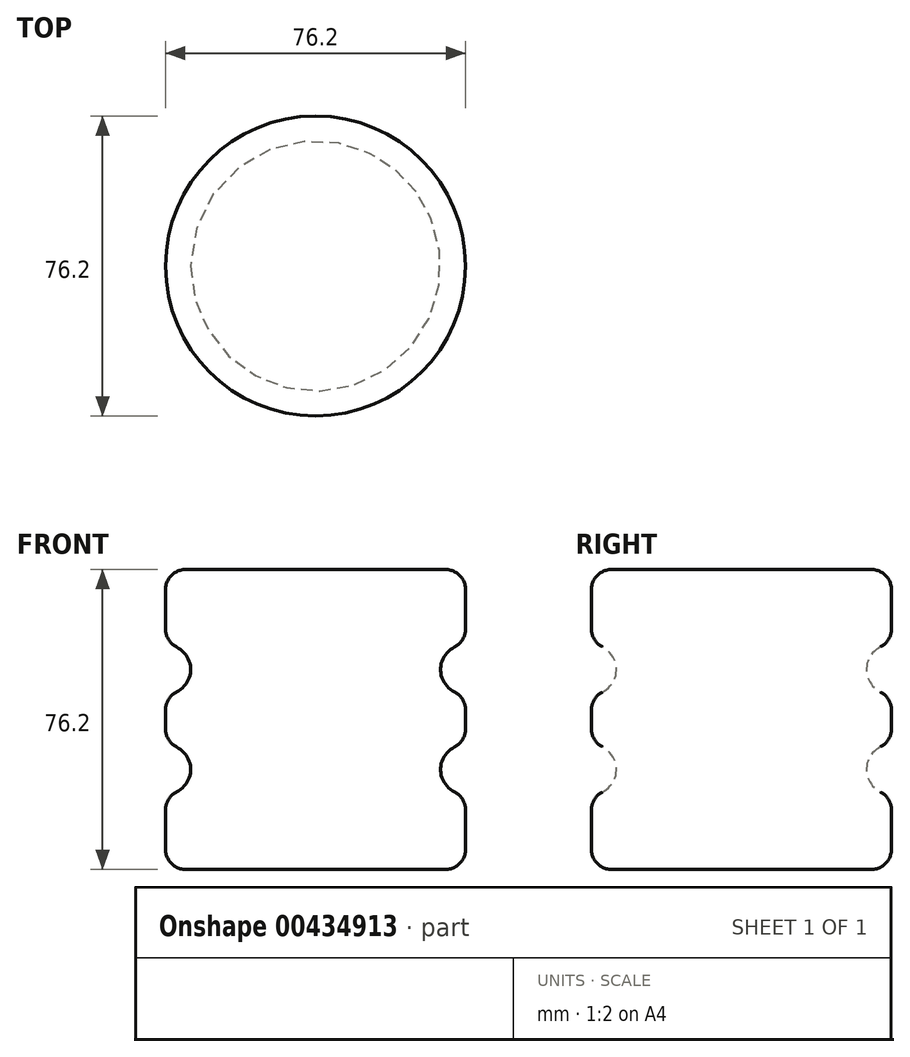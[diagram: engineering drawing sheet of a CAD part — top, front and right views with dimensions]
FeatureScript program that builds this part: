
annotation { "Feature Type Name" : "Feature", "Feature Type Description" : "" }
export const myFeature = defineFeature(function(context is Context, id is Id, definition is map)
    precondition{}
    {
        {
            var Q0;
            Q0=qCreatedBy(makeId("Front.planeOp"),FACE);
            var sketch = newSketch(context, id + "F0", { "sketchPlane" : qUnion([Q0])});
            skLineSegment(sketch, "E0.bottom", {"start": v(0, 0) * mm, "end": v(-38.1, 0) * mm});
            skLineSegment(sketch, "E0.top", {"start": v(0, 76.2) * mm, "end": v(-38.1, 76.2) * mm});
            skLineSegment(sketch, "E0.left", {"start": v(0, 0) * mm, "end": v(0, 19.05) * mm});
            skLineSegment(sketch, "E0.right", {"start": v(-38.1, 0) * mm, "end": v(-38.1, 76.2) * mm});
            skArc(sketch, "E1", {"start": v(0, 57.15) * mm, "mid": v(-6.35, 50.8) * mm, "end": v(0, 44.45) * mm});
            skArc(sketch, "E2", {"start": v(0, 31.75) * mm, "mid": v(-6.35, 25.4) * mm, "end": v(0, 19.05) * mm});
            skLineSegment(sketch, "E3.trimOffspring", {"start": v(0, 57.15) * mm, "end": v(0, 76.2) * mm});
            skLineSegment(sketch, "E4.trimOffspring", {"start": v(0, 31.75) * mm, "end": v(0, 44.45) * mm});
            skSolve(sketch);
        }
        {
            var Q0;
            Q0 = qSketchRegion(id + "F0", true);
            var Q1;
            Q1=sQuery(id+"F0.wireOp",EDGE,"E0.right");
            revolve(context, id + "F1", {"entities" : qUnion([Q0]), "axis" : qUnion([Q1]), "revolveType" : RevolveType.FULL});
        }
        {
            var Q0;
            Q0=makeQuery(id+"F1.opRevolve","SWEPT_EDGE",EDGE,{"disambiguationData":[OSD([sQuery(id+"F0.wireOp",EDGE,"E1"),sQuery(id+"F0.wireOp",EDGE,"E3.trimOffspring")])]});
            var Q1;
            Q1=makeQuery(id+"F1.opRevolve","SWEPT_EDGE",EDGE,{"disambiguationData":[OSD([sQuery(id+"F0.wireOp",EDGE,"E0.top"),sQuery(id+"F0.wireOp",EDGE,"E3.trimOffspring")])]});
            var Q2;
            Q2=makeQuery(id+"F1.opRevolve","SWEPT_EDGE",EDGE,{"disambiguationData":[OSD([sQuery(id+"F0.wireOp",EDGE,"E1"),sQuery(id+"F0.wireOp",EDGE,"E4.trimOffspring")])]});
            var Q3;
            Q3=makeQuery(id+"F1.opRevolve","SWEPT_EDGE",EDGE,{"disambiguationData":[OSD([sQuery(id+"F0.wireOp",EDGE,"E2"),sQuery(id+"F0.wireOp",EDGE,"E4.trimOffspring")])]});
            var Q4;
            Q4=makeQuery(id+"F1.opRevolve","SWEPT_EDGE",EDGE,{"disambiguationData":[OSD([sQuery(id+"F0.wireOp",EDGE,"E0.left"),sQuery(id+"F0.wireOp",EDGE,"E2")])]});
            var Q5;
            Q5=makeQuery(id+"F1.opRevolve","SWEPT_EDGE",EDGE,{"disambiguationData":[OSD([sQuery(id+"F0.wireOp",EDGE,"E0.bottom"),sQuery(id+"F0.wireOp",EDGE,"E0.left")])]});
            fillet(context, id + "F2", {"entities" : qUnion([Q0, Q1, Q2, Q3, Q4, Q5]), "radius" : 5.08 * mm, "tangentPropagation" : true, "allowEdgeOverflow" : false});
        }
    });
